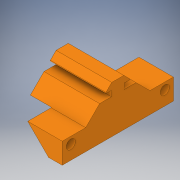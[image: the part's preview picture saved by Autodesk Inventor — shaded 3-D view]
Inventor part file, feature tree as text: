
AUTODESK INVENTOR PART (.ipt)
format: ipt  version: 2019 (Build 230136000, 136)  size: 189,440 bytes
history: native  units: in
note: dims shown in document units (in); Inventor stores cm internally (conversion verified against a paired STEP export)
features: sketch x4, extrude x3, chamfer x3, fillet x1, thicken_offset x1, hole x1, projected_geometry x1
ambient origin geometry x8: Origin, YZ Plane, XZ Plane, XY Plane, X Axis, Y Axis, Z Axis, Center Point
bodies: Body1 (feature_tree)
feature tree (14):
  extrude  "Extrusion2"  Depth=0.1in
  fillet  "Fillet1"  Radius=0.121in
  thicken_offset  "Thicken1"
  extrude  "Extrusion3"  Depth=0.442in
  extrude  "Extrusion4"  TaperAngle=135.0deg  [1 undecoded]
  chamfer  "Chamfer1"  Distance=0.218in
  chamfer  "Chamfer2"  Distance=1.0in
  chamfer  "Chamfer3"  Distance=0.01in
  hole  "Hole1"  [1 undecoded]
  sketch  "Sketch1"  dims[d1=0.655in d2=0.1in d9=0.121in]
  sketch  "Sketch2"  dims[d12=0.0in d15=0.442in d16=0.46in]
  sketch  "Sketch3"  dims[d20=135.0deg d21=135.0deg]
  projected_geometry  "Projected Loop1"
  sketch  "Sketch4"  dims[d26=0.115in d38=0.218in d41=1.0in d42=0.0in d43=0.01in d44=0.15in d45=0.15in d46=0.625in d47=0.25in d48=0.0in d49=2.0in d50=0.655in d51=0.6725in d52=0.375in d53=0.25in d54=0.0in d55=0.25in d56=0.125in d57=45.0deg d58=0.375in d59=0.125in d60=45.0deg d61=0.375in d62=0.125in d63=45.0deg d64=0.154in d66=0.154in d68=0.165in d69=0.75in d70=0.375in d71=0.25in d72=0.5635in d73=1.0in d74=0.8108in d75=0.154in d76=0.154in d77=0.23in d78=0.2125in]
note: 2 required parameter values undecoded (feature->parameter linkage not recoverable at this tier; creation-order binding heuristic only, values carry confidence <= 0.55)
